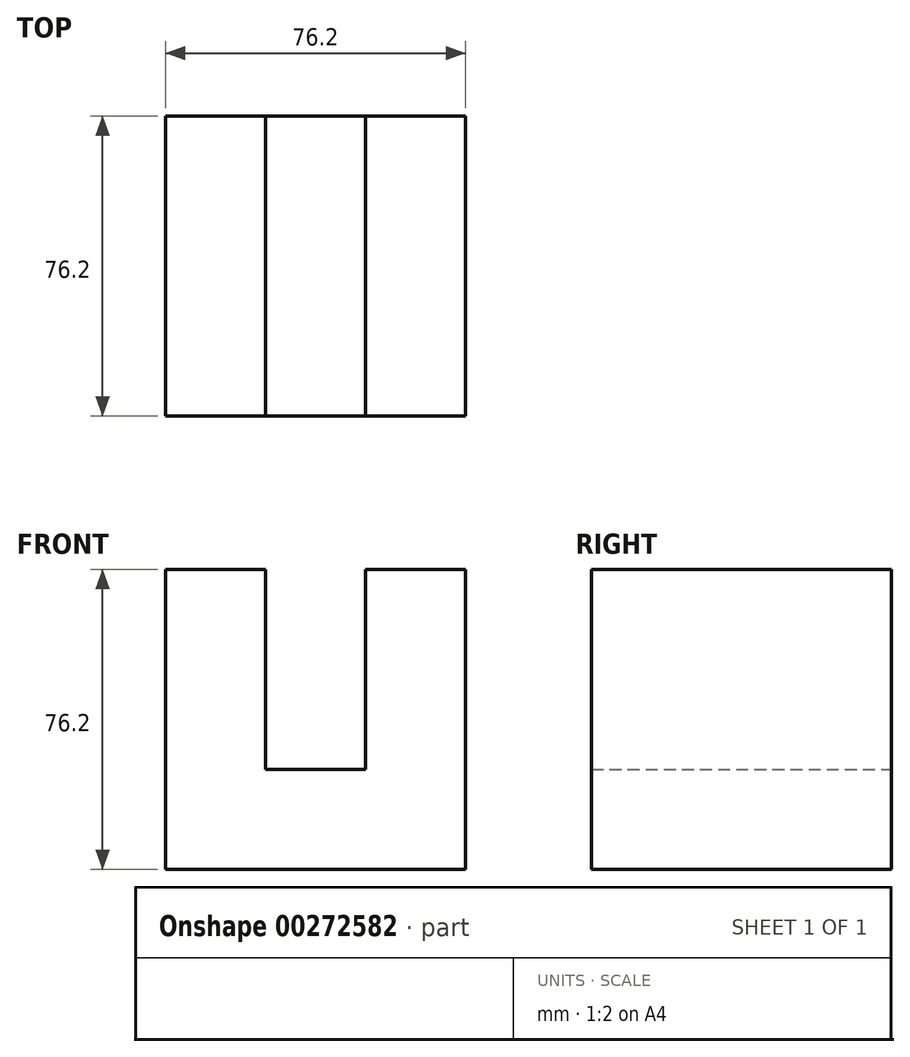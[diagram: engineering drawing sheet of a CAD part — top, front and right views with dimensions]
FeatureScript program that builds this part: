
annotation { "Feature Type Name" : "Feature", "Feature Type Description" : "" }
export const myFeature = defineFeature(function(context is Context, id is Id, definition is map)
    precondition{}
    {
        {
            var Q0;
            Q0=qCreatedBy(makeId("Front.planeOp"),FACE);
            var sketch = newSketch(context, id + "F0", { "sketchPlane" : qUnion([Q0])});
            skLineSegment(sketch, "E0", {"start": v(-50.8, -33.04) * mm, "end": v(25.4, -33.04) * mm});
            skLineSegment(sketch, "E1", {"start": v(25.4, -33.04) * mm, "end": v(25.4, 43.16) * mm});
            skLineSegment(sketch, "E2", {"start": v(25.4, 43.16) * mm, "end": v(0, 43.16) * mm});
            skLineSegment(sketch, "E3", {"start": v(0, 43.16) * mm, "end": v(0, -7.64) * mm});
            skLineSegment(sketch, "E4", {"start": v(0, -7.64) * mm, "end": v(-25.4, -7.64) * mm});
            skLineSegment(sketch, "E5", {"start": v(-25.4, -7.64) * mm, "end": v(-25.4, 43.16) * mm});
            skLineSegment(sketch, "E6", {"start": v(-25.4, 43.16) * mm, "end": v(-50.8, 43.16) * mm});
            skLineSegment(sketch, "E7", {"start": v(-50.8, 43.16) * mm, "end": v(-50.8, -33.04) * mm});
            skSolve(sketch);
        }
        {
            var Q0;
            Q0=makeQuery(id+"F0.imprint","IMPRINT",FACE,{"disambiguationData":[TD([[makeQuery(id+"F0.imprint","IMPRINT",EDGE,{"derivedFrom":sQuery(id+"F0.wireOp",EDGE,"E0")}),1.0]])]});
            extrude(context, id + "F1", {"entities" : qUnion([Q0]), "depth" : 76.2 * mm});
        }
    });
